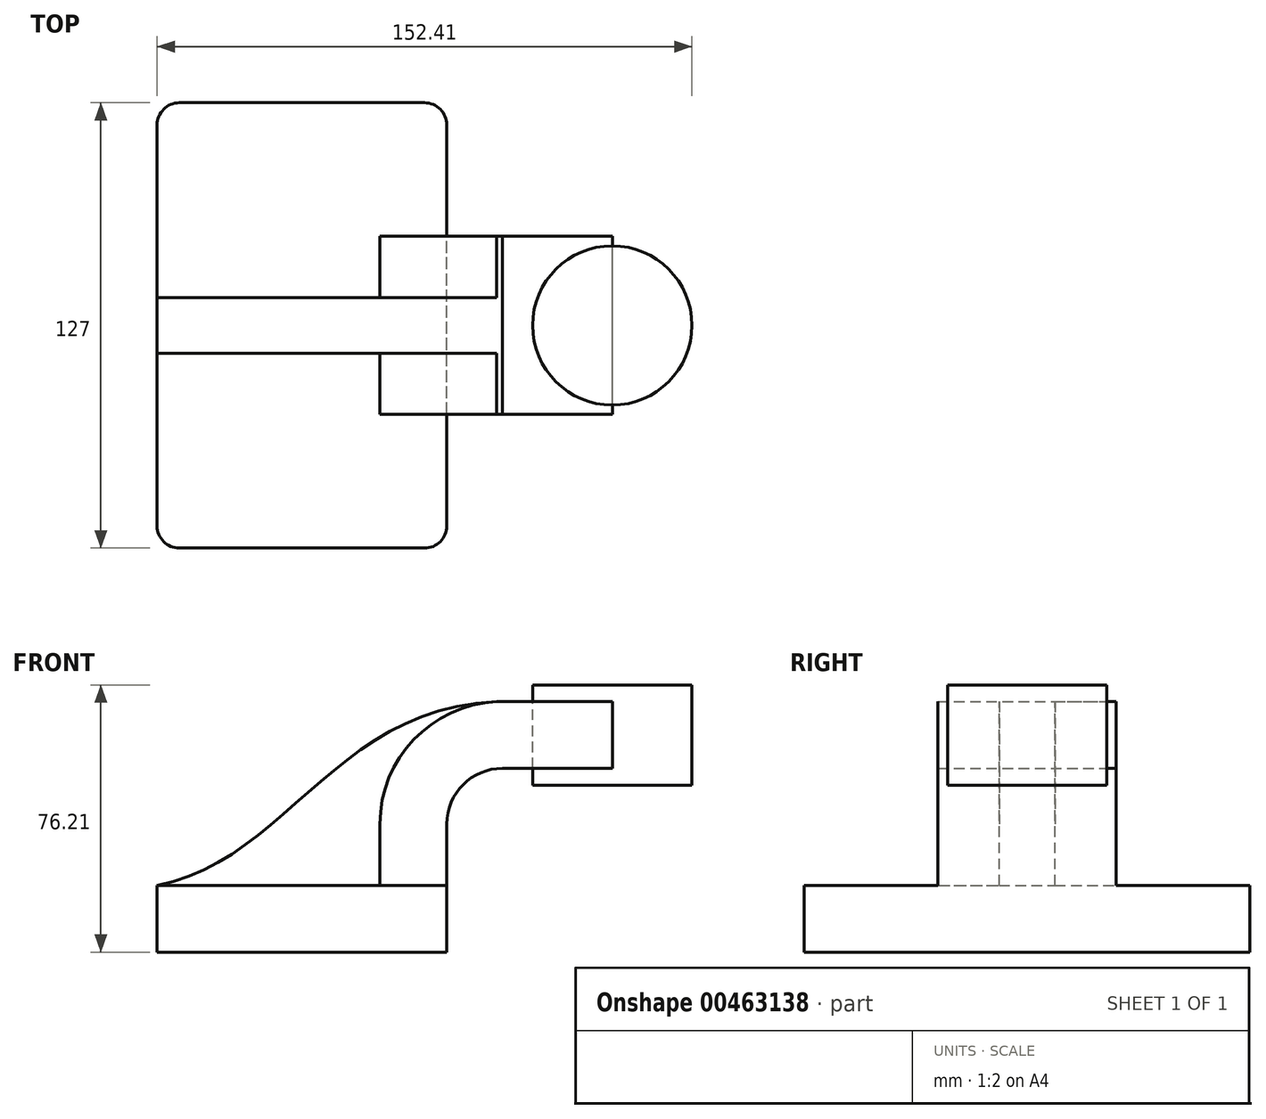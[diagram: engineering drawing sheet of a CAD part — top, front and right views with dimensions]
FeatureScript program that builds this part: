
annotation { "Feature Type Name" : "Feature", "Feature Type Description" : "" }
export const myFeature = defineFeature(function(context is Context, id is Id, definition is map)
    precondition{}
    {
        {
            var Q0;
            Q0=qCreatedBy(makeId("Front.planeOp"),FACE);
            var sketch = newSketch(context, id + "F0", { "sketchPlane" : qUnion([Q0])});
            skLineSegment(sketch, "E0.bottom", {"start": v(41.28, -9.52) * mm, "end": v(-41.28, -9.53) * mm});
            skLineSegment(sketch, "E0.top", {"start": v(41.27, 9.53) * mm, "end": v(-41.28, 9.53) * mm});
            skLineSegment(sketch, "E0.left", {"start": v(41.28, -9.52) * mm, "end": v(41.28, 9.53) * mm});
            skLineSegment(sketch, "E0.right", {"start": v(-41.28, -9.53) * mm, "end": v(-41.28, 9.53) * mm});
            skPoint(sketch, "E0.middle", {"position": v(0, 0) * mm});
            skLineSegment(sketch, "E1.bottom", {"start": v(111.12, 38.1) * mm, "end": v(60.32, 38.1) * mm});
            skLineSegment(sketch, "E1.top", {"start": v(111.12, 66.68) * mm, "end": v(60.32, 66.68) * mm});
            skLineSegment(sketch, "E1.left", {"start": v(111.12, 38.1) * mm, "end": v(111.12, 66.68) * mm});
            skLineSegment(sketch, "E1.right", {"start": v(60.32, 38.1) * mm, "end": v(60.32, 66.68) * mm});
            skPoint(sketch, "E1.middle", {"position": v(85.72, 52.39) * mm});
            skPoint(sketch, "E2.endSnap0", {"position": v(60.32, 52.39) * mm});
            skLineSegment(sketch, "E3", {"start": v(41.27, 9.53) * mm, "end": v(41.27, 27) * mm});
            skArc(sketch, "E4", {"start": v(41.27, 27) * mm, "mid": v(45.92, 38.23) * mm, "end": v(57.15, 42.88) * mm});
            skLineSegment(sketch, "E5", {"start": v(57.15, 42.88) * mm, "end": v(88.43, 42.88) * mm});
            skLineSegment(sketch, "E6.0", {"start": v(57.15, 61.93) * mm, "end": v(88.43, 61.93) * mm});
            skArc(sketch, "E6.1", {"start": v(22.23, 27) * mm, "mid": v(32.45, 51.7) * mm, "end": v(57.15, 61.93) * mm});
            skLineSegment(sketch, "E6.2", {"start": v(22.22, 9.53) * mm, "end": v(22.22, 27) * mm});
            skLineSegment(sketch, "E7", {"start": v(88.43, 66.68) * mm, "end": v(88.43, 38.1) * mm});
            skFitSpline(sketch, "E8", {"points": [v(-41.28, 9.52) * mm, v(57.15, 61.93) * mm], "startDerivative": vector(111.35, 20.66) * mm, "endDerivative": vector(141.92, 1.86) * mm});
            skSolve(sketch);
        }
        {
            var Q0;
            Q0=makeQuery(id+"F0.imprint","IMPRINT",FACE,{"disambiguationData":[TD([[makeQuery(id+"F0.imprint","IMPRINT",EDGE,{"derivedFrom":sQuery(id+"F0.wireOp",EDGE,"E0.bottom")}),-1.0]])]});
            extrude(context, id + "F1", {"entities" : qUnion([Q0]), "endBound" : BoundingType.SYMMETRIC, "depth" : 127 * mm});
        }
        {
            var Q0;
            {var subQ1=sQuery(id+"F0.wireOp",EDGE,"E3");Q0=makeQuery(id+"F0.imprint","IMPRINT",FACE,{"disambiguationData":[TD([[makeQuery(id+"F0.imprint","IMPRINT",EDGE,{"derivedFrom":subQ1}),1.0]])]});}
            var Q1;
            {var subQ0=sQuery(id+"F0.wireOp",EDGE,"E5");var subQ1=sQuery(id+"F0.wireOp",EDGE,"E1.right");var subQ2=makeQuery(id+"F0.imprint","INTERSECT",VERTEX,{"derivedFrom":[subQ1,subQ0]});Q1=makeQuery(id+"F0.imprint","IMPRINT",FACE,{"disambiguationData":[TD([[makeQuery(id+"F0.imprint","IMPRINT",EDGE,{"disambiguationData":[TD([[subQ2,-1.0]])],"derivedFrom":subQ1}),-1.0]])]});}
            extrude(context, id + "F2", {"entities" : qUnion([Q0, Q1]), "operationType" : NewBodyOperationType.ADD, "endBound" : BoundingType.SYMMETRIC, "depth" : 50.8 * mm});
        }
        {
            var Q0;
            {var subQ3=sQuery(id+"F0.wireOp",EDGE,"E6.2");Q0=makeQuery(id+"F0.imprint","IMPRINT",FACE,{"disambiguationData":[TD([[makeQuery(id+"F0.imprint","IMPRINT",EDGE,{"derivedFrom":subQ3}),1.0]])]});}
            extrude(context, id + "F3", {"entities" : qUnion([Q0]), "operationType" : NewBodyOperationType.ADD, "endBound" : BoundingType.SYMMETRIC, "depth" : 15.88 * mm});
        }
        {
            var Q0;
            {var subQ0=sQuery(id+"F0.wireOp",EDGE,"E1.left");Q0=makeQuery(id+"F0.imprint","IMPRINT",FACE,{"disambiguationData":[TD([[makeQuery(id+"F0.imprint","IMPRINT",EDGE,{"derivedFrom":subQ0}),1.0]])]});}
            var Q1;
            Q1=sQuery(id+"F0.wireOp",EDGE,"E7");
            revolve(context, id + "F4", {"entities" : qUnion([Q0]), "axis" : qUnion([Q1]), "revolveType" : RevolveType.FULL});
        }
        {
            var Q0;
            Q0=makeQuery(id+"F1.opExtrude","CAP_EDGE",EDGE,{"disambiguationData":[OSD([sQuery(id+"F0.wireOp",EDGE,"E0.right")])],"isStart":false});
            var Q1;
            Q1=makeQuery(id+"F1.opExtrude","CAP_EDGE",EDGE,{"disambiguationData":[OSD([sQuery(id+"F0.wireOp",EDGE,"E0.left")])],"isStart":false});
            var Q2;
            Q2=makeQuery(id+"F1.opExtrude","CAP_EDGE",EDGE,{"disambiguationData":[OSD([sQuery(id+"F0.wireOp",EDGE,"E0.left")])],"isStart":true});
            var Q3;
            Q3=makeQuery(id+"F1.opExtrude","CAP_EDGE",EDGE,{"disambiguationData":[OSD([sQuery(id+"F0.wireOp",EDGE,"E0.right")])],"isStart":true});
            fillet(context, id + "F5", {"entities" : qUnion([Q0, Q1, Q2, Q3]), "radius" : 6.35 * mm, "tangentPropagation" : true, "allowEdgeOverflow" : false});
        }
    });
